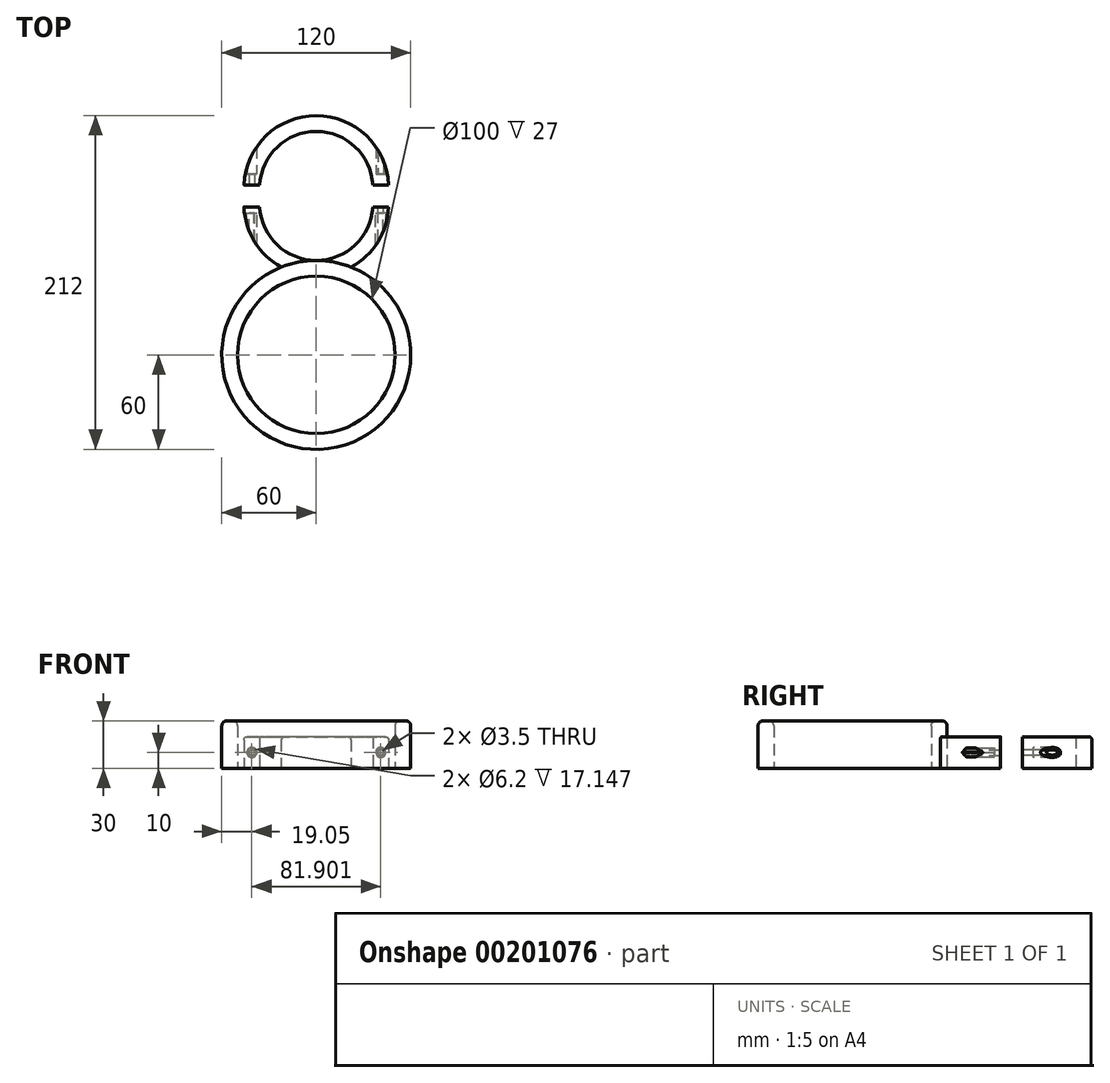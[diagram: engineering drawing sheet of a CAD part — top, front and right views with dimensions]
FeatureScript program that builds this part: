
annotation { "Feature Type Name" : "Feature", "Feature Type Description" : "" }
export const myFeature = defineFeature(function(context is Context, id is Id, definition is map)
    precondition{}
    {
        {
            var Q0;
            Q0=qCreatedBy(makeId("Top.planeOp"),FACE);
            var sketch = newSketch(context, id + "F0", { "sketchPlane" : qUnion([Q0])});
            skCircle(sketch, "E0", {"center": v(0, 0) * mm, "radius": 50 * mm});
            skCircle(sketch, "E1", {"center": v(0, 0) * mm, "radius": 60 * mm});
            skArc(sketch, "E2", {"start": v(-46, 96) * mm, "mid": v(0, 50) * mm, "end": v(46, 96) * mm});
            skArc(sketch, "E3", {"start": v(-36, 96) * mm, "mid": v(0, 60) * mm, "end": v(36, 96) * mm});
            skLineSegment(sketch, "E4", {"start": v(36, 96) * mm, "end": v(46, 96) * mm});
            skLineSegment(sketch, "E5", {"start": v(-36, 96) * mm, "end": v(-46, 96) * mm});
            skArc(sketch, "E6", {"start": v(46, 106) * mm, "mid": v(0, 152) * mm, "end": v(-46, 106) * mm});
            skArc(sketch, "E7", {"start": v(36, 106) * mm, "mid": v(0, 142) * mm, "end": v(-36, 106) * mm});
            skLineSegment(sketch, "E8", {"start": v(-36, 106) * mm, "end": v(-46, 106) * mm});
            skLineSegment(sketch, "E9", {"start": v(36, 106) * mm, "end": v(46, 106) * mm});
            skLineSegment(sketch, "E10", {"start": v(-45.96, 94) * mm, "end": v(-35.94, 94) * mm});
            skLineSegment(sketch, "E11", {"start": v(-45.96, 108) * mm, "end": v(-35.94, 108) * mm});
            skLineSegment(sketch, "E12.MirrorCS", {"start": v(45.96, 94) * mm, "end": v(35.94, 94) * mm});
            skLineSegment(sketch, "E13.MirrorCS", {"start": v(45.96, 108) * mm, "end": v(35.94, 108) * mm});
            skSolve(sketch);
        }
        {
            var Q0;
            {var subQ5=sQuery(id+"F0.wireOp",EDGE,"E12.MirrorCS");Q0=makeQuery(id+"F0.imprint","IMPRINT",FACE,{"disambiguationData":[TD([[makeQuery(id+"F0.imprint","IMPRINT",EDGE,{"derivedFrom":subQ5}),1.0]])]});}
            var Q1;
            {var subQ5=sQuery(id+"F0.wireOp",EDGE,"E10");Q1=makeQuery(id+"F0.imprint","IMPRINT",FACE,{"disambiguationData":[TD([[makeQuery(id+"F0.imprint","IMPRINT",EDGE,{"derivedFrom":subQ5}),-1.0]])]});}
            var Q2;
            {var subQ0=sQuery(id+"F0.wireOp",EDGE,"E11");Q2=makeQuery(id+"F0.imprint","IMPRINT",FACE,{"disambiguationData":[TD([[makeQuery(id+"F0.imprint","IMPRINT",EDGE,{"derivedFrom":subQ0}),1.0]])]});}
            extrude(context, id + "F1", {"entities" : qUnion([Q0, Q1, Q2]), "depth" : 20 * mm, "offsetDistance" : 25 * mm});
        }
        {
            var Q0;
            {var subQ0=sQuery(id+"F0.wireOp",EDGE,"E0");Q0=makeQuery(id+"F0.imprint","IMPRINT",FACE,{"disambiguationData":[TD([[makeQuery(id+"F0.imprint","IMPRINT",EDGE,{"derivedFrom":subQ0}),-1.0]])]});}
            var Q1;
            {var subQ0=sQuery(id+"F0.wireOp",EDGE,"E1");var subQ1=makeQuery(id+"F0.imprint","INTERSECT",VERTEX,{"derivedFrom":[subQ0,sQuery(id+"F0.wireOp",EDGE,"E3")]});Q1=makeQuery(id+"F0.imprint","IMPRINT",FACE,{"disambiguationData":[TD([[makeQuery(id+"F0.imprint","IMPRINT",EDGE,{"disambiguationData":[TD([[subQ1,1.0]])],"derivedFrom":subQ0}),1.0]])]});}
            extrude(context, id + "F2", {"entities" : qUnion([Q0, Q1]), "operationType" : NewBodyOperationType.ADD, "depth" : 30 * mm, "offsetDistance" : 25 * mm});
        }
        {
            var Q0;
            Q0=makeQuery(id+"F1.opExtrude","SWEPT_FACE",FACE,{"disambiguationData":[OSD([sQuery(id+"F0.wireOp",EDGE,"E12.MirrorCS")])]});
            var sketch = newSketch(context, id + "F3", { "sketchPlane" : qUnion([Q0])});
            skLineSegment(sketch, "E14", {"start": v(-45.96, 10) * mm, "end": v(-35.94, 10) * mm, "construction": true});
            skLineSegment(sketch, "E15", {"start": v(-40.95, 20) * mm, "end": v(-40.95, 0) * mm, "construction": true});
            skCircle(sketch, "E16", {"center": v(-40.95, 10) * mm, "radius": 1.75 * mm});
            skCircle(sketch, "E17.cCircle", {"center": v(-40.95, 10) * mm, "radius": 2.77 * mm, "construction": true});
            skLineSegment(sketch, "E17.0", {"start": v(-39.35, 7.23) * mm, "end": v(-42.55, 7.23) * mm});
            skLineSegment(sketch, "E17.1", {"start": v(-42.55, 7.23) * mm, "end": v(-44.15, 10) * mm});
            skLineSegment(sketch, "E17.2", {"start": v(-44.15, 10) * mm, "end": v(-42.55, 12.77) * mm});
            skLineSegment(sketch, "E17.3", {"start": v(-42.55, 12.77) * mm, "end": v(-39.35, 12.77) * mm});
            skLineSegment(sketch, "E17.4", {"start": v(-39.35, 12.77) * mm, "end": v(-37.75, 10) * mm});
            skLineSegment(sketch, "E17.5", {"start": v(-37.75, 10) * mm, "end": v(-39.35, 7.23) * mm});
            skPoint(sketch, "E17.0.midPoint", {"position": v(-40.95, 7.23) * mm});
            skCircle(sketch, "E18.MirrorC", {"center": v(40.95, 10) * mm, "radius": 2.77 * mm, "construction": true});
            skLineSegment(sketch, "E19.MirrorCS", {"start": v(39.35, 12.77) * mm, "end": v(37.75, 10) * mm});
            skLineSegment(sketch, "E20.MirrorCS", {"start": v(42.55, 7.23) * mm, "end": v(44.15, 10) * mm});
            skLineSegment(sketch, "E21.MirrorCS", {"start": v(39.35, 7.23) * mm, "end": v(42.55, 7.23) * mm});
            skLineSegment(sketch, "E22.MirrorCS", {"start": v(37.75, 10) * mm, "end": v(39.35, 7.23) * mm});
            skPoint(sketch, "E23.MirrorP", {"position": v(40.95, 7.23) * mm});
            skLineSegment(sketch, "E24.MirrorCS", {"start": v(42.55, 12.77) * mm, "end": v(39.35, 12.77) * mm});
            skCircle(sketch, "E25.MirrorC", {"center": v(40.95, 10) * mm, "radius": 1.75 * mm});
            skLineSegment(sketch, "E26.MirrorCS", {"start": v(44.15, 10) * mm, "end": v(42.55, 12.77) * mm});
            skSolve(sketch);
        }
        {
            var Q0;
            Q0=makeQuery(id+"F3.imprint","IMPRINT",FACE,{"disambiguationData":[TD([[makeQuery(id+"F3.imprint","IMPRINT",EDGE,{"derivedFrom":sQuery(id+"F3.wireOp",EDGE,"E16")}),1.0]])]});
            var Q1;
            Q1=makeQuery(id+"F3.imprint","IMPRINT",FACE,{"disambiguationData":[TD([[makeQuery(id+"F3.imprint","IMPRINT",EDGE,{"derivedFrom":sQuery(id+"F3.wireOp",EDGE,"E25.MirrorC")}),-1.0]])]});
            extrude(context, id + "F4", {"entities" : qUnion([Q0, Q1]), "operationType" : NewBodyOperationType.REMOVE, "oppositeDirection" : true, "depth" : 23.9 * mm, "offsetDistance" : 25 * mm});
        }
        {
            var Q0;
            Q0=makeQuery(id+"F3.imprint","IMPRINT",FACE,{"disambiguationData":[TD([[makeQuery(id+"F3.imprint","IMPRINT",EDGE,{"derivedFrom":sQuery(id+"F3.wireOp",EDGE,"E16")}),-1.0]])]});
            var Q1;
            Q1=makeQuery(id+"F3.imprint","IMPRINT",FACE,{"disambiguationData":[TD([[makeQuery(id+"F3.imprint","IMPRINT",EDGE,{"derivedFrom":sQuery(id+"F3.wireOp",EDGE,"E20.MirrorCS")}),1.0]])]});
            extrude(context, id + "F5", {"entities" : qUnion([Q0, Q1]), "operationType" : NewBodyOperationType.REMOVE, "oppositeDirection" : true, "depth" : 25 * mm, "offsetDistance" : 25 * mm});
        }
        {
            var Q0;
            Q0=makeQuery(id+"F3.imprint","IMPRINT",FACE,{"disambiguationData":[TD([[makeQuery(id+"F3.imprint","IMPRINT",EDGE,{"derivedFrom":sQuery(id+"F3.wireOp",EDGE,"E16")}),-1.0]])]});
            var Q1;
            Q1=makeQuery(id+"F3.imprint","IMPRINT",FACE,{"disambiguationData":[TD([[makeQuery(id+"F3.imprint","IMPRINT",EDGE,{"derivedFrom":sQuery(id+"F3.wireOp",EDGE,"E20.MirrorCS")}),1.0]])]});
            extrude(context, id + "F6", {"entities" : qUnion([Q0, Q1]), "operationType" : NewBodyOperationType.ADD, "oppositeDirection" : true, "depth" : 4 * mm, "offsetDistance" : 25 * mm});
        }
        {
            var Q0;
            Q0=makeQuery(id+"F1.opExtrude","SWEPT_FACE",FACE,{"disambiguationData":[OSD([sQuery(id+"F0.wireOp",EDGE,"E13.MirrorCS")])]});
            var sketch = newSketch(context, id + "F7", { "sketchPlane" : qUnion([Q0])});
            skLineSegment(sketch, "E27", {"start": v(-45.96, 10) * mm, "end": v(-35.94, 10) * mm, "construction": true});
            skLineSegment(sketch, "E28", {"start": v(-40.95, 20) * mm, "end": v(-40.95, 0) * mm, "construction": true});
            skCircle(sketch, "E29", {"center": v(-40.95, 10) * mm, "radius": 1.75 * mm});
            skCircle(sketch, "E30.cCircle", {"center": v(-40.95, 10) * mm, "radius": 2.68 * mm, "construction": true});
            skLineSegment(sketch, "E30.0", {"start": v(-39.4, 7.32) * mm, "end": v(-42.5, 7.32) * mm});
            skLineSegment(sketch, "E30.1", {"start": v(-42.5, 7.32) * mm, "end": v(-44.05, 10) * mm});
            skLineSegment(sketch, "E30.2", {"start": v(-44.05, 10) * mm, "end": v(-42.5, 12.68) * mm});
            skLineSegment(sketch, "E30.3", {"start": v(-42.5, 12.68) * mm, "end": v(-39.4, 12.68) * mm});
            skLineSegment(sketch, "E30.4", {"start": v(-39.4, 12.68) * mm, "end": v(-37.85, 10) * mm});
            skLineSegment(sketch, "E30.5", {"start": v(-37.85, 10) * mm, "end": v(-39.4, 7.32) * mm});
            skPoint(sketch, "E30.0.midPoint", {"position": v(-40.95, 7.32) * mm});
            skPoint(sketch, "E31.MirrorP", {"position": v(40.95, 10) * mm});
            skLineSegment(sketch, "E32.MirrorCS", {"start": v(42.5, 12.68) * mm, "end": v(39.4, 12.68) * mm});
            skLineSegment(sketch, "E33.MirrorCS", {"start": v(37.85, 10) * mm, "end": v(39.4, 7.32) * mm});
            skCircle(sketch, "E34.MirrorC", {"center": v(40.95, 10) * mm, "radius": 1.75 * mm});
            skLineSegment(sketch, "E35.MirrorCS", {"start": v(44.05, 10) * mm, "end": v(42.5, 12.68) * mm});
            skLineSegment(sketch, "E36.MirrorCS", {"start": v(39.4, 7.32) * mm, "end": v(42.5, 7.32) * mm});
            skLineSegment(sketch, "E37.MirrorCS", {"start": v(39.4, 12.68) * mm, "end": v(37.85, 10) * mm});
            skPoint(sketch, "E38.MirrorP", {"position": v(40.95, 7.32) * mm});
            skCircle(sketch, "E39.MirrorC", {"center": v(40.95, 10) * mm, "radius": 2.68 * mm, "construction": true});
            skLineSegment(sketch, "E40.MirrorCS", {"start": v(42.5, 7.32) * mm, "end": v(44.05, 10) * mm});
            skCircle(sketch, "E41", {"center": v(-40.95, 10) * mm, "radius": 3.1 * mm});
            skCircle(sketch, "E42", {"center": v(40.95, 10) * mm, "radius": 3.1 * mm});
            skSolve(sketch);
        }
        {
            var Q0;
            Q0=makeQuery(id+"F7.imprint","IMPRINT",FACE,{"disambiguationData":[TD([[makeQuery(id+"F7.imprint","IMPRINT",EDGE,{"derivedFrom":sQuery(id+"F7.wireOp",EDGE,"E29")}),1.0]])]});
            var Q1;
            Q1=makeQuery(id+"F7.imprint","IMPRINT",FACE,{"disambiguationData":[TD([[makeQuery(id+"F7.imprint","IMPRINT",EDGE,{"derivedFrom":sQuery(id+"F7.wireOp",EDGE,"E34.MirrorC")}),-1.0]])]});
            extrude(context, id + "F8", {"entities" : qUnion([Q0, Q1]), "operationType" : NewBodyOperationType.REMOVE, "oppositeDirection" : true, "depth" : 25 * mm, "offsetDistance" : 25 * mm});
        }
        {
            var Q0;
            {var subQ0=sQuery(id+"F7.wireOp",EDGE,"E30.4");Q0=makeQuery(id+"F7.imprint","IMPRINT",FACE,{"disambiguationData":[TD([[makeQuery(id+"F7.imprint","IMPRINT",EDGE,{"derivedFrom":subQ0}),1.0]])]});}
            var Q1;
            Q1=makeQuery(id+"F7.imprint","IMPRINT",FACE,{"disambiguationData":[TD([[makeQuery(id+"F7.imprint","IMPRINT",EDGE,{"derivedFrom":sQuery(id+"F7.wireOp",EDGE,"E29")}),-1.0]])]});
            var Q2;
            {var subQ0=sQuery(id+"F7.wireOp",EDGE,"E30.3");Q2=makeQuery(id+"F7.imprint","IMPRINT",FACE,{"disambiguationData":[TD([[makeQuery(id+"F7.imprint","IMPRINT",EDGE,{"derivedFrom":subQ0}),1.0]])]});}
            var Q3;
            {var subQ0=sQuery(id+"F7.wireOp",EDGE,"E30.2");Q3=makeQuery(id+"F7.imprint","IMPRINT",FACE,{"disambiguationData":[TD([[makeQuery(id+"F7.imprint","IMPRINT",EDGE,{"derivedFrom":subQ0}),1.0]])]});}
            var Q4;
            {var subQ0=sQuery(id+"F7.wireOp",EDGE,"E30.1");Q4=makeQuery(id+"F7.imprint","IMPRINT",FACE,{"disambiguationData":[TD([[makeQuery(id+"F7.imprint","IMPRINT",EDGE,{"derivedFrom":subQ0}),1.0]])]});}
            var Q5;
            {var subQ0=sQuery(id+"F7.wireOp",EDGE,"E30.0");Q5=makeQuery(id+"F7.imprint","IMPRINT",FACE,{"disambiguationData":[TD([[makeQuery(id+"F7.imprint","IMPRINT",EDGE,{"derivedFrom":subQ0}),1.0]])]});}
            var Q6;
            {var subQ0=sQuery(id+"F7.wireOp",EDGE,"E30.5");Q6=makeQuery(id+"F7.imprint","IMPRINT",FACE,{"disambiguationData":[TD([[makeQuery(id+"F7.imprint","IMPRINT",EDGE,{"derivedFrom":subQ0}),1.0]])]});}
            var Q7;
            {var subQ0=sQuery(id+"F7.wireOp",EDGE,"E37.MirrorCS");Q7=makeQuery(id+"F7.imprint","IMPRINT",FACE,{"disambiguationData":[TD([[makeQuery(id+"F7.imprint","IMPRINT",EDGE,{"derivedFrom":subQ0}),-1.0]])]});}
            var Q8;
            Q8=makeQuery(id+"F7.imprint","IMPRINT",FACE,{"disambiguationData":[TD([[makeQuery(id+"F7.imprint","IMPRINT",EDGE,{"derivedFrom":sQuery(id+"F7.wireOp",EDGE,"E32.MirrorCS")}),1.0]])]});
            var Q9;
            {var subQ0=sQuery(id+"F7.wireOp",EDGE,"E32.MirrorCS");Q9=makeQuery(id+"F7.imprint","IMPRINT",FACE,{"disambiguationData":[TD([[makeQuery(id+"F7.imprint","IMPRINT",EDGE,{"derivedFrom":subQ0}),-1.0]])]});}
            var Q10;
            {var subQ0=sQuery(id+"F7.wireOp",EDGE,"E35.MirrorCS");Q10=makeQuery(id+"F7.imprint","IMPRINT",FACE,{"disambiguationData":[TD([[makeQuery(id+"F7.imprint","IMPRINT",EDGE,{"derivedFrom":subQ0}),-1.0]])]});}
            var Q11;
            {var subQ0=sQuery(id+"F7.wireOp",EDGE,"E40.MirrorCS");Q11=makeQuery(id+"F7.imprint","IMPRINT",FACE,{"disambiguationData":[TD([[makeQuery(id+"F7.imprint","IMPRINT",EDGE,{"derivedFrom":subQ0}),-1.0]])]});}
            var Q12;
            {var subQ0=sQuery(id+"F7.wireOp",EDGE,"E33.MirrorCS");Q12=makeQuery(id+"F7.imprint","IMPRINT",FACE,{"disambiguationData":[TD([[makeQuery(id+"F7.imprint","IMPRINT",EDGE,{"derivedFrom":subQ0}),-1.0]])]});}
            var Q13;
            {var subQ0=sQuery(id+"F7.wireOp",EDGE,"E36.MirrorCS");Q13=makeQuery(id+"F7.imprint","IMPRINT",FACE,{"disambiguationData":[TD([[makeQuery(id+"F7.imprint","IMPRINT",EDGE,{"derivedFrom":subQ0}),-1.0]])]});}
            extrude(context, id + "F9", {"entities" : qUnion([Q0, Q1, Q2, Q3, Q4, Q5, Q6, Q7, Q8, Q9, Q10, Q11, Q12, Q13]), "operationType" : NewBodyOperationType.REMOVE, "oppositeDirection" : true, "depth" : 25 * mm, "offsetDistance" : 25 * mm});
        }
        {
            var Q0;
            Q0=makeQuery(id+"F7.imprint","IMPRINT",FACE,{"disambiguationData":[TD([[makeQuery(id+"F7.imprint","IMPRINT",EDGE,{"derivedFrom":sQuery(id+"F7.wireOp",EDGE,"E32.MirrorCS")}),1.0]])]});
            var Q1;
            {var subQ0=sQuery(id+"F7.wireOp",EDGE,"E37.MirrorCS");Q1=makeQuery(id+"F7.imprint","IMPRINT",FACE,{"disambiguationData":[TD([[makeQuery(id+"F7.imprint","IMPRINT",EDGE,{"derivedFrom":subQ0}),-1.0]])]});}
            var Q2;
            {var subQ0=sQuery(id+"F7.wireOp",EDGE,"E33.MirrorCS");Q2=makeQuery(id+"F7.imprint","IMPRINT",FACE,{"disambiguationData":[TD([[makeQuery(id+"F7.imprint","IMPRINT",EDGE,{"derivedFrom":subQ0}),-1.0]])]});}
            var Q3;
            {var subQ0=sQuery(id+"F7.wireOp",EDGE,"E36.MirrorCS");Q3=makeQuery(id+"F7.imprint","IMPRINT",FACE,{"disambiguationData":[TD([[makeQuery(id+"F7.imprint","IMPRINT",EDGE,{"derivedFrom":subQ0}),-1.0]])]});}
            var Q4;
            {var subQ0=sQuery(id+"F7.wireOp",EDGE,"E40.MirrorCS");Q4=makeQuery(id+"F7.imprint","IMPRINT",FACE,{"disambiguationData":[TD([[makeQuery(id+"F7.imprint","IMPRINT",EDGE,{"derivedFrom":subQ0}),-1.0]])]});}
            var Q5;
            {var subQ0=sQuery(id+"F7.wireOp",EDGE,"E35.MirrorCS");Q5=makeQuery(id+"F7.imprint","IMPRINT",FACE,{"disambiguationData":[TD([[makeQuery(id+"F7.imprint","IMPRINT",EDGE,{"derivedFrom":subQ0}),-1.0]])]});}
            var Q6;
            {var subQ0=sQuery(id+"F7.wireOp",EDGE,"E32.MirrorCS");Q6=makeQuery(id+"F7.imprint","IMPRINT",FACE,{"disambiguationData":[TD([[makeQuery(id+"F7.imprint","IMPRINT",EDGE,{"derivedFrom":subQ0}),-1.0]])]});}
            var Q7;
            {var subQ0=sQuery(id+"F7.wireOp",EDGE,"E30.4");Q7=makeQuery(id+"F7.imprint","IMPRINT",FACE,{"disambiguationData":[TD([[makeQuery(id+"F7.imprint","IMPRINT",EDGE,{"derivedFrom":subQ0}),1.0]])]});}
            var Q8;
            Q8=makeQuery(id+"F7.imprint","IMPRINT",FACE,{"disambiguationData":[TD([[makeQuery(id+"F7.imprint","IMPRINT",EDGE,{"derivedFrom":sQuery(id+"F7.wireOp",EDGE,"E29")}),-1.0]])]});
            var Q9;
            {var subQ0=sQuery(id+"F7.wireOp",EDGE,"E30.5");Q9=makeQuery(id+"F7.imprint","IMPRINT",FACE,{"disambiguationData":[TD([[makeQuery(id+"F7.imprint","IMPRINT",EDGE,{"derivedFrom":subQ0}),1.0]])]});}
            var Q10;
            {var subQ0=sQuery(id+"F7.wireOp",EDGE,"E30.0");Q10=makeQuery(id+"F7.imprint","IMPRINT",FACE,{"disambiguationData":[TD([[makeQuery(id+"F7.imprint","IMPRINT",EDGE,{"derivedFrom":subQ0}),1.0]])]});}
            var Q11;
            {var subQ0=sQuery(id+"F7.wireOp",EDGE,"E30.1");Q11=makeQuery(id+"F7.imprint","IMPRINT",FACE,{"disambiguationData":[TD([[makeQuery(id+"F7.imprint","IMPRINT",EDGE,{"derivedFrom":subQ0}),1.0]])]});}
            var Q12;
            {var subQ0=sQuery(id+"F7.wireOp",EDGE,"E30.2");Q12=makeQuery(id+"F7.imprint","IMPRINT",FACE,{"disambiguationData":[TD([[makeQuery(id+"F7.imprint","IMPRINT",EDGE,{"derivedFrom":subQ0}),1.0]])]});}
            var Q13;
            {var subQ0=sQuery(id+"F7.wireOp",EDGE,"E30.3");Q13=makeQuery(id+"F7.imprint","IMPRINT",FACE,{"disambiguationData":[TD([[makeQuery(id+"F7.imprint","IMPRINT",EDGE,{"derivedFrom":subQ0}),1.0]])]});}
            extrude(context, id + "F10", {"entities" : qUnion([Q0, Q1, Q2, Q3, Q4, Q5, Q6, Q7, Q8, Q9, Q10, Q11, Q12, Q13]), "operationType" : NewBodyOperationType.ADD, "oppositeDirection" : true, "depth" : 7 * mm, "offsetDistance" : 25 * mm});
        }
        {
            var Q0;
            Q0=makeQuery(id+"F2.opExtrude","CAP_FACE",FACE,{"disambiguationData":[OSD([sQuery(id+"F0.wireOp",EDGE,"E0"),sQuery(id+"F0.wireOp",EDGE,"E1")])],"isStart":false});
            fillet(context, id + "F11", {"entities" : qUnion([Q0]), "tangentPropagation" : true, "radius" : 3 * mm, "defaultsChanged" : true, "vertexSettings" : [], "allowEdgeOverflow" : false});
        }
        {
            var Q0;
            {var subQ0=sQuery(id+"F0.wireOp",EDGE,"E2");Q0=makeQuery(id+"F1.opExtrude","CAP_EDGE",EDGE,{"disambiguationData":[OSD([subQ0]),TDD([makeQuery(id+"F0.imprint","IMPRINT",EDGE,{"disambiguationData":[TD([[makeQuery(id+"F0.imprint","INTERSECT",VERTEX,{"derivedFrom":[subQ0,sQuery(id+"F0.wireOp",EDGE,"E12.MirrorCS")]}),1.0]])],"derivedFrom":subQ0})])],"isStart":false});}
            var Q1;
            {var subQ0=sQuery(id+"F0.wireOp",EDGE,"E2");Q1=makeQuery(id+"F1.opExtrude","CAP_EDGE",EDGE,{"disambiguationData":[OSD([subQ0]),TDD([makeQuery(id+"F0.imprint","IMPRINT",EDGE,{"disambiguationData":[TD([[makeQuery(id+"F0.imprint","INTERSECT",VERTEX,{"derivedFrom":[subQ0,sQuery(id+"F0.wireOp",EDGE,"E10")]}),-1.0]])],"derivedFrom":subQ0})])],"isStart":false});}
            var Q2;
            Q2=makeQuery(id+"F1.opExtrude","CAP_EDGE",EDGE,{"disambiguationData":[OSD([sQuery(id+"F0.wireOp",EDGE,"E6")])],"isStart":false});
            fillet(context, id + "F12", {"entities" : qUnion([Q0, Q1, Q2]), "tangentPropagation" : true, "radius" : 2 * mm, "defaultsChanged" : false, "vertexSettings" : [], "allowEdgeOverflow" : false});
        }
    });
